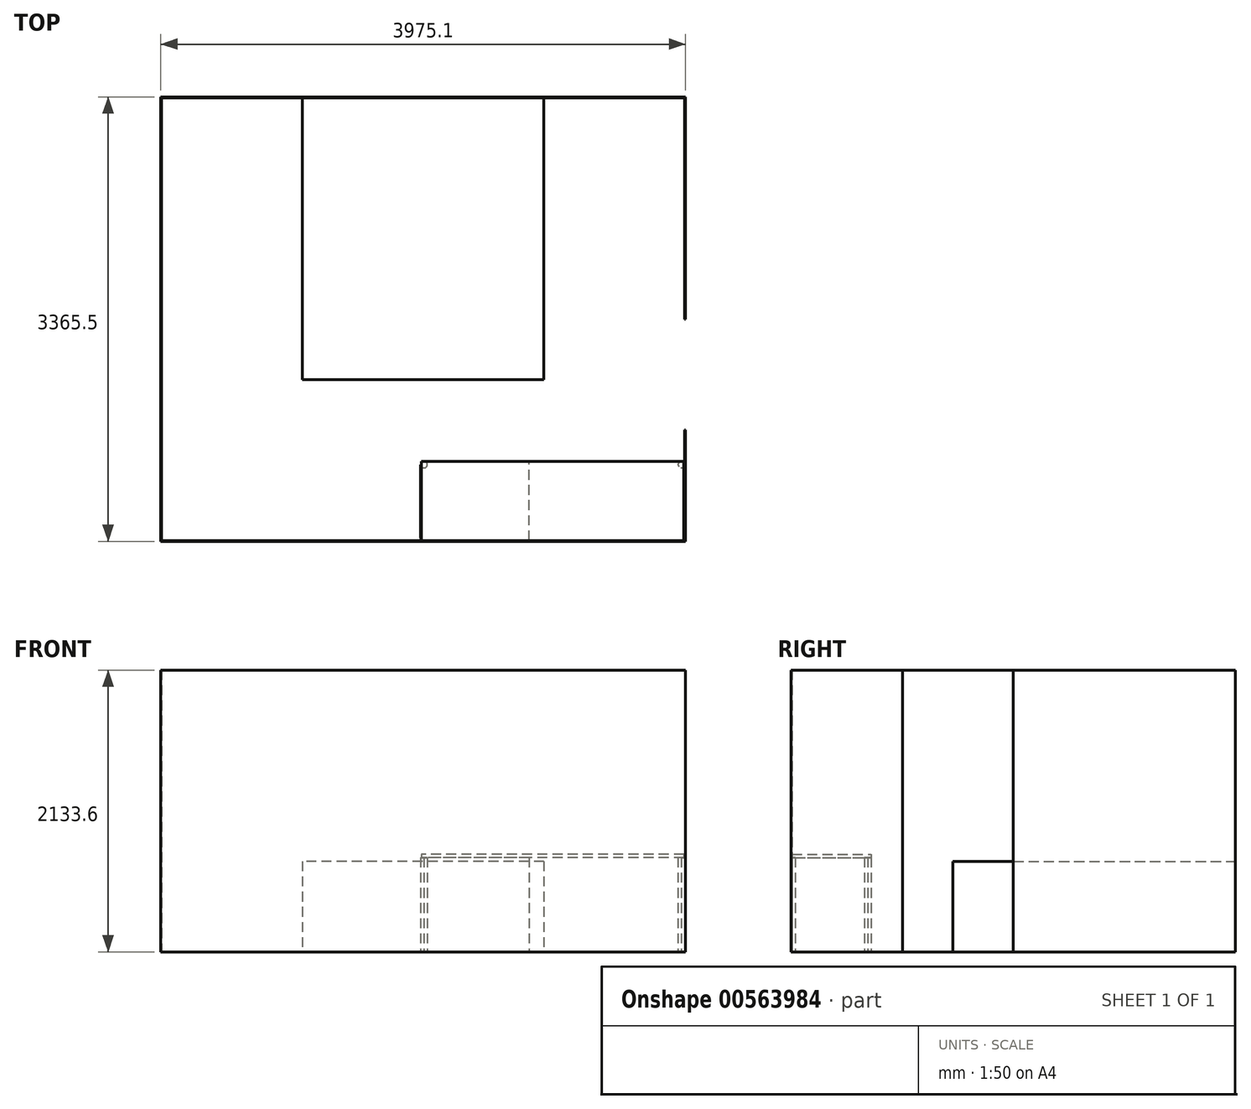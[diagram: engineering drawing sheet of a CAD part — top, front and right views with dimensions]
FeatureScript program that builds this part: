
annotation { "Feature Type Name" : "Feature", "Feature Type Description" : "" }
export const myFeature = defineFeature(function(context is Context, id is Id, definition is map)
    precondition{}
    {
        {
            var Q0;
            Q0=qCreatedBy(makeId("Top.planeOp"),FACE);
            var sketch = newSketch(context, id + "F0", { "sketchPlane" : qUnion([Q0])});
            skLineSegment(sketch, "E0.bottom", {"start": v(914.4, -1066.8) * mm, "end": v(-914.4, -1066.8) * mm});
            skLineSegment(sketch, "E0.top", {"start": v(914.4, 1066.8) * mm, "end": v(-914.4, 1066.8) * mm});
            skLineSegment(sketch, "E0.left", {"start": v(914.4, -1066.8) * mm, "end": v(914.4, 1066.8) * mm});
            skLineSegment(sketch, "E0.right", {"start": v(-914.4, -1066.8) * mm, "end": v(-914.4, 1066.8) * mm});
            skPoint(sketch, "E0.middle", {"position": v(0, 0) * mm});
            skLineSegment(sketch, "E1", {"start": v(0, 0) * mm, "end": v(0, 1066.8) * mm, "construction": true});
            skSolve(sketch);
        }
        {
            var Q0;
            Q0=makeQuery(id+"F0.imprint","IMPRINT",FACE,{"disambiguationData":[TD([[makeQuery(id+"F0.imprint","IMPRINT",EDGE,{"derivedFrom":sQuery(id+"F0.wireOp",EDGE,"E0.bottom")}),-1.0]])]});
            extrude(context, id + "F1", {"entities" : qUnion([Q0]), "depth" : 685.8 * mm, "offsetDistance" : 25.4 * mm});
        }
        {
            var Q0;
            Q0=qCreatedBy(makeId("Top.planeOp"),FACE);
            var sketch = newSketch(context, id + "F2", { "sketchPlane" : qUnion([Q0])});
            skLineSegment(sketch, "E2.bottom", {"start": v(-1981.2, 1066.8) * mm, "end": v(1981.2, 1066.8) * mm});
            skLineSegment(sketch, "E2.top", {"start": v(-1981.2, -2286) * mm, "end": v(-101.6, -2286) * mm});
            skLineSegment(sketch, "E2.left", {"start": v(-1981.2, 1066.8) * mm, "end": v(-1981.2, -2286) * mm});
            skLineSegment(sketch, "E2.right", {"start": v(1981.2, 1066.8) * mm, "end": v(1981.2, -609.6) * mm});
            skLineSegment(sketch, "E3", {"start": v(1981.2, -1447.8) * mm, "end": v(1981.2, -2286) * mm});
            skLineSegment(sketch, "E4", {"start": v(1981.2, -609.6) * mm, "end": v(1981.2, -1447.8) * mm});
            skLineSegment(sketch, "E5", {"start": v(-101.6, -2286) * mm, "end": v(-19.81, -2286) * mm});
            skLineSegment(sketch, "E6.bottom", {"start": v(1981.2, -2286) * mm, "end": v(-19.81, -2286) * mm});
            skLineSegment(sketch, "E6.top", {"start": v(1981.2, -1685.93) * mm, "end": v(-19.81, -1685.93) * mm});
            skLineSegment(sketch, "E6.left", {"start": v(1981.2, -2286) * mm, "end": v(1981.2, -1685.93) * mm});
            skLineSegment(sketch, "E6.right", {"start": v(-19.81, -2286) * mm, "end": v(-19.81, -1685.93) * mm});
            skCircle(sketch, "E7", {"center": v(5.59, -2260.6) * mm, "radius": 25.4 * mm});
            skLineSegment(sketch, "E8", {"start": v(-19.81, -1985.96) * mm, "end": v(1981.2, -1985.96) * mm, "construction": true});
            skLineSegment(sketch, "E9", {"start": v(-19.81, -2286) * mm, "end": v(1981.2, -2286) * mm});
            skLineSegment(sketch, "E10", {"start": v(980.7, -2286) * mm, "end": v(980.7, -1685.93) * mm, "construction": true});
            skCircle(sketch, "E11.MirrorC", {"center": v(5.59, -1711.33) * mm, "radius": 25.4 * mm});
            skCircle(sketch, "E12.MirrorC", {"center": v(1955.8, -2260.6) * mm, "radius": 25.4 * mm});
            skCircle(sketch, "E13.MirrorC", {"center": v(1955.8, -1711.33) * mm, "radius": 25.4 * mm});
            skLineSegment(sketch, "E14.bottom", {"start": v(1160.08, -2286) * mm, "end": v(801.3, -2286) * mm});
            skLineSegment(sketch, "E14.top", {"start": v(1160.08, -1685.93) * mm, "end": v(801.3, -1685.93) * mm});
            skLineSegment(sketch, "E14.left", {"start": v(1160.08, -2286) * mm, "end": v(1160.08, -1685.93) * mm});
            skLineSegment(sketch, "E14.right", {"start": v(801.3, -2286) * mm, "end": v(801.3, -1685.93) * mm});
            skPoint(sketch, "E14.middle", {"position": v(980.7, -1985.96) * mm});
            skLineSegment(sketch, "E15.0", {"start": v(1987.55, 1073.15) * mm, "end": v(1987.55, -609.6) * mm});
            skLineSegment(sketch, "E15.1", {"start": v(-1987.55, 1073.15) * mm, "end": v(1987.55, 1073.15) * mm});
            skLineSegment(sketch, "E15.2", {"start": v(-1987.55, 1073.15) * mm, "end": v(-1987.55, -2292.35) * mm});
            skLineSegment(sketch, "E15.3", {"start": v(1987.55, -1447.8) * mm, "end": v(1987.55, -2292.35) * mm});
            skLineSegment(sketch, "E15.4", {"start": v(-19.81, -2292.35) * mm, "end": v(1987.55, -2292.35) * mm});
            skLineSegment(sketch, "E15.5", {"start": v(-101.6, -2292.35) * mm, "end": v(-19.81, -2292.35) * mm});
            skLineSegment(sketch, "E15.6", {"start": v(-1987.55, -2292.35) * mm, "end": v(-101.6, -2292.35) * mm});
            skLineSegment(sketch, "E16", {"start": v(1981.2, -1447.8) * mm, "end": v(1987.55, -1447.8) * mm});
            skLineSegment(sketch, "E17", {"start": v(1981.2, -609.6) * mm, "end": v(1987.55, -609.6) * mm});
            skSolve(sketch);
        }
        {
            var Q0;
            Q0=makeQuery(id+"F2.imprint","IMPRINT",FACE,{"disambiguationData":[TD([[makeQuery(id+"F2.imprint","IMPRINT",EDGE,{"derivedFrom":sQuery(id+"F2.wireOp",EDGE,"E14.bottom")}),-1.0]])]});
            var Q1;
            {var subQ0=sQuery(id+"F2.wireOp",EDGE,"E12.MirrorC");var subQ1=makeQuery(id+"F2.imprint","INTERSECT",VERTEX,{"derivedFrom":[sQuery(id+"F2.wireOp",EDGE,"E6.left"),subQ0]});Q1=makeQuery(id+"F2.imprint","IMPRINT",FACE,{"disambiguationData":[TD([[makeQuery(id+"F2.imprint","IMPRINT",EDGE,{"disambiguationData":[TD([[subQ1,-1.0]])],"derivedFrom":subQ0}),-1.0]])]});}
            var Q2;
            {var subQ0=sQuery(id+"F2.wireOp",EDGE,"E13.MirrorC");var subQ1=makeQuery(id+"F2.imprint","INTERSECT",VERTEX,{"derivedFrom":[sQuery(id+"F2.wireOp",EDGE,"E6.left"),subQ0]});Q2=makeQuery(id+"F2.imprint","IMPRINT",FACE,{"disambiguationData":[TD([[makeQuery(id+"F2.imprint","IMPRINT",EDGE,{"disambiguationData":[TD([[subQ1,-1.0]])],"derivedFrom":subQ0}),1.0]])]});}
            var Q3;
            {var subQ0=sQuery(id+"F2.wireOp",EDGE,"E7");var subQ1=makeQuery(id+"F2.imprint","INTERSECT",VERTEX,{"derivedFrom":[subQ0,sQuery(id+"F2.wireOp",EDGE,"E9")]});Q3=makeQuery(id+"F2.imprint","IMPRINT",FACE,{"disambiguationData":[TD([[makeQuery(id+"F2.imprint","IMPRINT",EDGE,{"disambiguationData":[TD([[subQ1,1.0]])],"derivedFrom":subQ0}),1.0]])]});}
            var Q4;
            {var subQ0=sQuery(id+"F2.wireOp",EDGE,"E11.MirrorC");var subQ1=makeQuery(id+"F2.imprint","INTERSECT",VERTEX,{"derivedFrom":[sQuery(id+"F2.wireOp",EDGE,"E6.top"),subQ0]});Q4=makeQuery(id+"F2.imprint","IMPRINT",FACE,{"disambiguationData":[TD([[makeQuery(id+"F2.imprint","IMPRINT",EDGE,{"disambiguationData":[TD([[subQ1,1.0]])],"derivedFrom":subQ0}),-1.0]])]});}
            extrude(context, id + "F3", {"entities" : qUnion([Q0, Q1, Q2, Q3, Q4]), "depth" : 714.38 * mm, "offsetDistance" : 25.4 * mm});
        }
        {
            var Q0;
            Q0=makeQuery(id+"F3.opExtrude","CAP_FACE",FACE,{"disambiguationData":[OSD([sQuery(id+"F2.wireOp",EDGE,"E14.bottom"),sQuery(id+"F2.wireOp",EDGE,"E14.top"),sQuery(id+"F2.wireOp",EDGE,"E14.left"),sQuery(id+"F2.wireOp",EDGE,"E14.right")])],"isStart":false});
            var sketch = newSketch(context, id + "F4", { "sketchPlane" : qUnion([Q0])});
            skLineSegment(sketch, "E18.bottom", {"start": v(1974.29, -2286) * mm, "end": v(-12.9, -2286) * mm});
            skLineSegment(sketch, "E18.top", {"start": v(1974.29, -1685.93) * mm, "end": v(-12.9, -1685.93) * mm});
            skLineSegment(sketch, "E18.left", {"start": v(1974.29, -2286) * mm, "end": v(1974.29, -1685.93) * mm});
            skLineSegment(sketch, "E18.right", {"start": v(-12.9, -2286) * mm, "end": v(-12.9, -1685.93) * mm});
            skPoint(sketch, "E18.middle", {"position": v(980.7, -1985.96) * mm});
            skPoint(sketch, "E18.middle.positionSnap0", {"position": v(980.7, -2286) * mm});
            skPoint(sketch, "E18.middle.positionSnap1", {"position": v(1160.08, -1985.96) * mm});
            skPoint(sketch, "E18.cornerSnap0", {"position": v(980.7, -2286) * mm});
            skPoint(sketch, "E18.centerSnap0", {"position": v(980.7, -2286) * mm});
            skPoint(sketch, "E18.centerSnap1", {"position": v(1160.08, -1985.96) * mm});
            skSolve(sketch);
        }
        {
            var Q0;
            Q0 = qSketchRegion(id + "F4", true);
            extrude(context, id + "F5", {"entities" : qUnion([Q0]), "depth" : 25.4 * mm, "offsetDistance" : 25.4 * mm});
        }
        {
            var Q0;
            Q0=makeQuery(id+"F2.imprint","IMPRINT",FACE,{"disambiguationData":[TD([[makeQuery(id+"F2.imprint","IMPRINT",EDGE,{"derivedFrom":sQuery(id+"F2.wireOp",EDGE,"E2.bottom")}),1.0]])]});
            extrude(context, id + "F6", {"entities" : qUnion([Q0]), "depth" : 2133.6 * mm, "offsetDistance" : 25.4 * mm});
        }
    });
